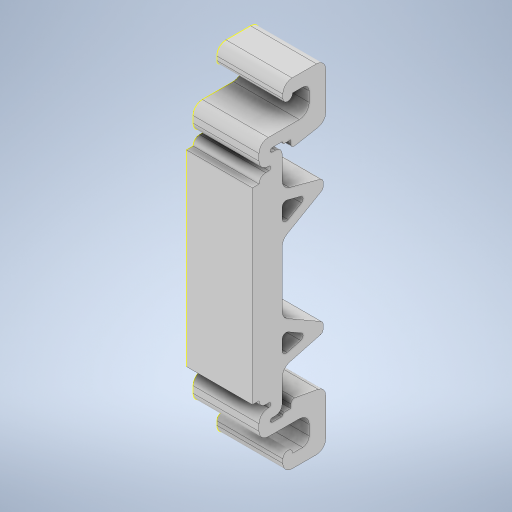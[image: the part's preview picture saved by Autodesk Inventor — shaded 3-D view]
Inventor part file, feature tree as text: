
AUTODESK INVENTOR PART (.ipt)
format: ipt  version: 2023 (Build 270158030, 158C)  size: 687,104 bytes
history: native  units: mm
features: other x4, extrude x2, sketch x2, projected_geometry x2, mirror x1
ambient origin geometry x8: Origin, YZ Plane, XZ Plane, XY Plane, X Axis, Y Axis, Z Axis, Center Point
bodies: Body1 (feature_tree), Body2 (feature_tree)
feature tree (11):
  other  "DIN-rail"
  other  "Blocks"
  extrude  "Extrusion5"  Depth=1.0mm
  extrude  "Extrusion6"  Depth=7.3mm
  mirror  "Mirror2"
  sketch  "Sketch7"  dims[d5=35.0mm d8=7.3mm d9=1.0mm d10=1.0mm d11=2.0mm d12=2.0mm d13=12.7mm d15=12.7mm d16=4.8mm d17=4.8mm d20=1.0mm d21=1.0mm d22=2.0mm d63=3.0mm d68=23.446722mm d71=0.937247mm d73=0.268963mm d74=0.352771mm d79=1.536323mm d85=0.790525mm d87=1.178422mm d88=0.790667mm d89=1.583516mm d90=5.132142mm d92=2.277882mm d93=2.745808mm d95=1.718388mm d96=0.72523mm d97=3.434383mm d99=1.223642mm d100=0.420939mm d101=1.2mm d102=0.8mm d103=1.8mm d104=0.8mm d105=2.6mm d106=0.10359mm d107=2.0mm d108=0.2mm d109=1.0mm d110=0.9mm d111=0.453644mm d112=1.2mm d113=1.4mm d114=0.037497mm d115=0.017085mm d116=0.527749mm d117=0.098913mm d118=0.689958mm d119=0.668213mm d120=0.705542mm d121=0.541172mm d122=1.737399mm d123=0.201916mm d124=0.5mm d125=0.302867mm d126=1.178422mm d127=3.970876mm d128=0.664321mm d129=1.031647mm d130=0.660389mm d131=0.064915mm d132=1.807627mm d133=1.565015mm d134=0.929795mm d136=0.743817mm d138=0.348214mm d139=0.310128mm d140=0.916882mm d141=2.209313mm d142=0.166244mm d143=0.176385mm d144=0.33806mm d145=0.652404mm d147=0.433822mm d148=1.6mm d149=0.56mm d150=1.034228mm d151=3.0mm d152=1.4mm d153=0.514445mm d154=0.593437mm d155=6.438638mm d156=0.946159mm d157=0.175634mm d158=0.264169mm d159=1.4mm d160=1.0mm d162=2.1mm d163=2.3mm d179=10.0mm d180=0.0mm d259=2.5mm d268=6.0mm d269=2.0mm d270=4.0mm d279=3.0mm d283=1.5mm d290=1.5mm d291=0.75mm d293=1.0mm d295=1.0mm d296=10.0mm d297=0.0mm d298=75.0deg d299=60.0deg d300=0.2mm d301=1.4mm d303=1.5mm d304=1.5mm d305=1.5mm d306=1.5mm d307=0.5mm d310=0.4mm d320=0.2mm d322=0.1mm d333=0.1mm d334=0.2mm d338=2.0mm d339=3.0mm d340=0.6mm d341=0.6mm d342=1.6mm d343=1.6mm d344=1.4mm d345=1.4mm d346=0.3mm d348=3.5mm d349=2.0mm d350=1.0mm d351=0.3mm d354=0.2mm d355=0.6mm d356=1.2mm d357=0.5mm d358=1.4mm d359=1.4mm d360=0.6mm d361=2.0mm]
  other  "DIN-rail-clip-generic-V1.0"
  sketch  "Sketch6"  dims[d0=1.0mm d1=1.0mm]
  other  "DIN-clip"
  projected_geometry  "Projected Loop3"
  projected_geometry  "Projected Loop4"
